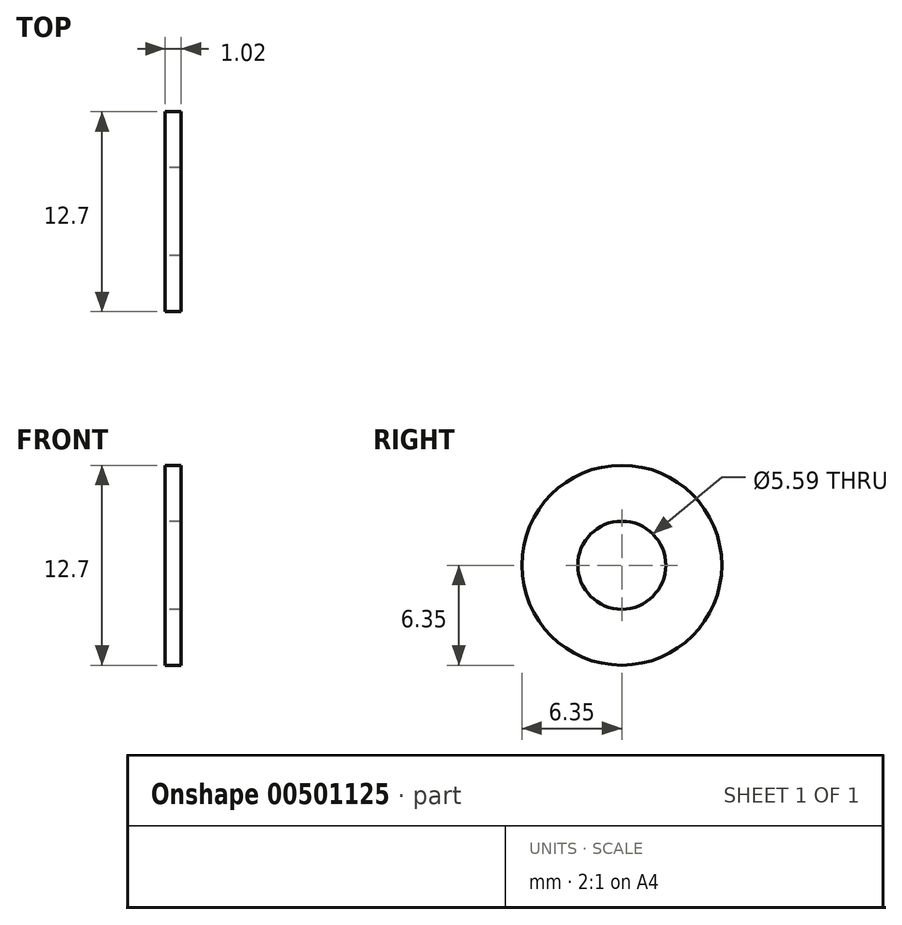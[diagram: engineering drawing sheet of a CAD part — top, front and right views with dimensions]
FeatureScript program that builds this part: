
annotation { "Feature Type Name" : "Feature", "Feature Type Description" : "" }
export const myFeature = defineFeature(function(context is Context, id is Id, definition is map)
    precondition{}
    {
        {
            var Q0;
            Q0=qCreatedBy(makeId("Right.planeOp"),FACE);
            var sketch = newSketch(context, id + "F0", { "sketchPlane" : qUnion([Q0])});
            skCircle(sketch, "E0", {"center": v(0, 0) * mm, "radius": 6.35 * mm});
            skCircle(sketch, "E1", {"center": v(0, 0) * mm, "radius": 2.8 * mm});
            skSolve(sketch);
        }
        {
            var Q0;
            Q0=qSketchRegion(id+"F0",true);
            extrude(context, id + "F1", {"entities" : qUnion([Q0]), "depth" : 1.02 * mm});
        }
    });
